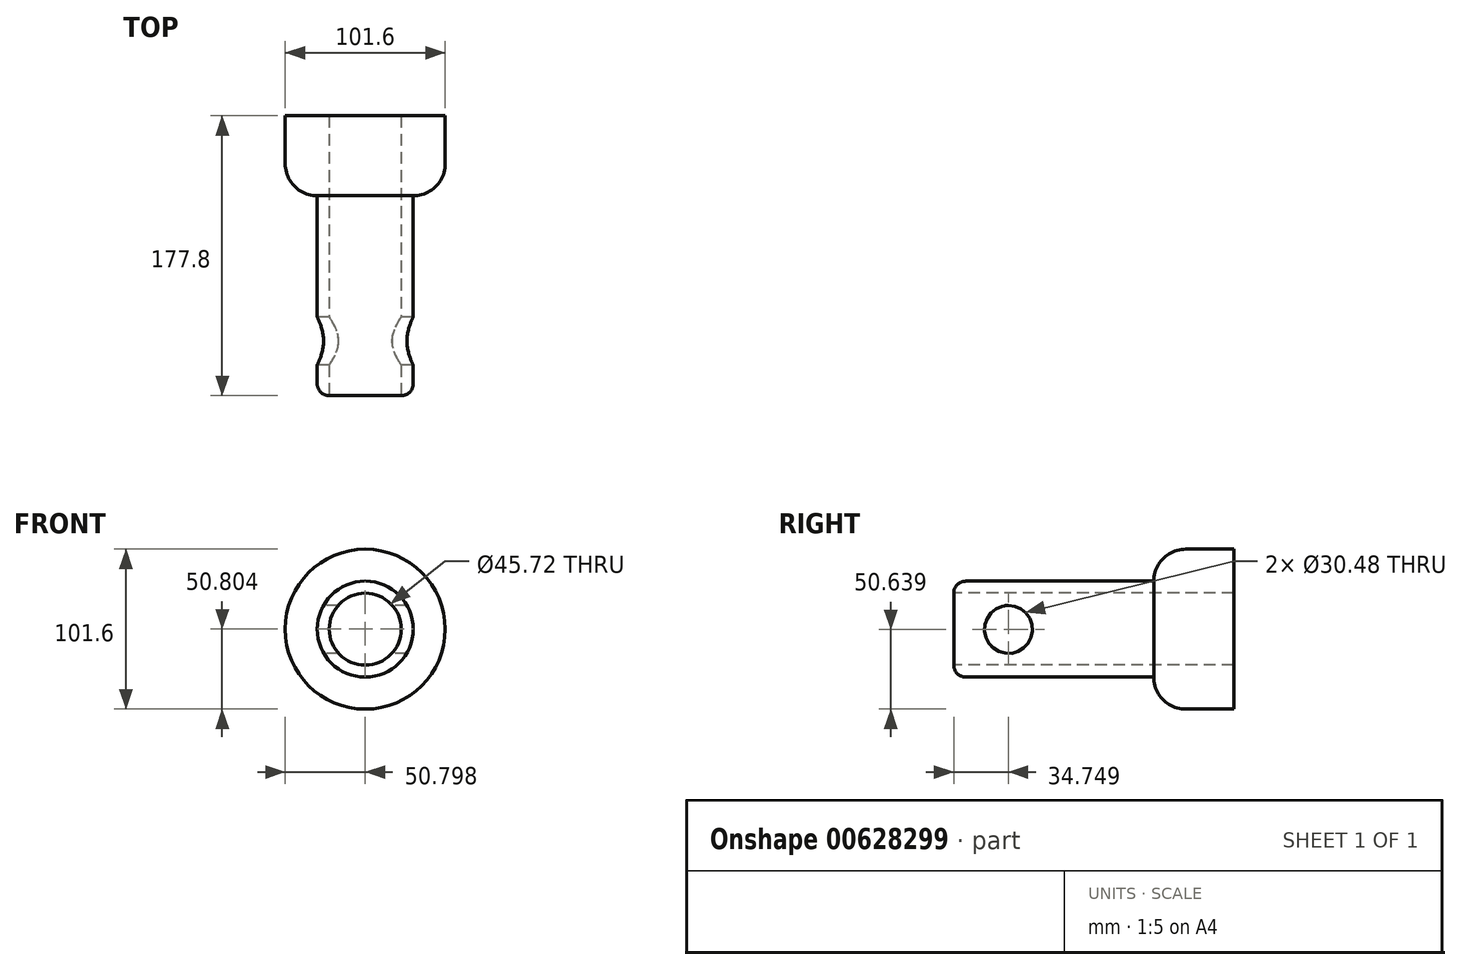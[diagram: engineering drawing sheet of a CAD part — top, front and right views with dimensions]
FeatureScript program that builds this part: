
annotation { "Feature Type Name" : "Feature", "Feature Type Description" : "" }
export const myFeature = defineFeature(function(context is Context, id is Id, definition is map)
    precondition{}
    {
        {
            var Q0;
            Q0=qCreatedBy(makeId("Front.planeOp"),FACE);
            var sketch = newSketch(context, id + "F0", { "sketchPlane" : qUnion([Q0])});
            skCircle(sketch, "E0", {"center": v(-16.63, 18.24) * mm, "radius": 50.8 * mm});
            skSolve(sketch);
        }
        {
            var Q0;
            Q0=makeQuery(id+"F0.imprint","IMPRINT",FACE,{"disambiguationData":[TD([[makeQuery(id+"F0.imprint","IMPRINT",EDGE,{"derivedFrom":sQuery(id+"F0.wireOp",EDGE,"E0")}),1.0]])]});
            extrude(context, id + "F1", {"entities" : qUnion([Q0]), "depth" : 50.8 * mm, "offsetDistance" : 25.4 * mm});
        }
        {
            var Q0;
            Q0=makeQuery(id+"F1.opExtrude","CAP_EDGE",EDGE,{"disambiguationData":[OSD([sQuery(id+"F0.wireOp",EDGE,"E0")])],"isStart":false});
            fillet(context, id + "F2", {"entities" : qUnion([Q0]), "radius" : 20.32 * mm, "tangentPropagation" : true, "allowEdgeOverflow" : false});
        }
        {
            var Q0;
            Q0=makeQuery(id+"F1.opExtrude","CAP_FACE",FACE,{"disambiguationData":[OSD([sQuery(id+"F0.wireOp",EDGE,"E0")])],"isStart":false});
            extrude(context, id + "F3", {"entities" : qUnion([Q0]), "operationType" : NewBodyOperationType.ADD, "depth" : 127 * mm, "offsetDistance" : 25.4 * mm});
        }
        {
            var Q0;
            Q0=makeQuery(id+"F3.opExtrude","CAP_EDGE",EDGE,{"disambiguationData":[OSD([sQuery(id+"F0.wireOp",EDGE,"E0")])],"isStart":false});
            fillet(context, id + "F4", {"entities" : qUnion([Q0]), "radius" : 7.62 * mm, "tangentPropagation" : true, "allowEdgeOverflow" : false});
        }
        {
            var Q0;
            Q0=makeQuery(id+"F3.opExtrude","CAP_FACE",FACE,{"disambiguationData":[OSD([sQuery(id+"F0.wireOp",EDGE,"E0")])],"isStart":false});
            extrude(context, id + "F5", {"entities" : qUnion([Q0]), "operationType" : NewBodyOperationType.REMOVE, "oppositeDirection" : true, "depth" : 231.9 * mm, "offsetDistance" : 25.4 * mm});
        }
        {
            var Q0;
            Q0=qCreatedBy(makeId("Right.planeOp"),FACE);
            var sketch = newSketch(context, id + "F6", { "sketchPlane" : qUnion([Q0])});
            skCircle(sketch, "E1", {"center": v(-143.05, 18.08) * mm, "radius": 15.24 * mm});
            skSolve(sketch);
        }
        {
            var Q0;
            Q0 = qSketchRegion(id + "F6", true);
            extrude(context, id + "F7", {"entities" : qUnion([Q0]), "operationType" : NewBodyOperationType.REMOVE, "depth" : 114.3 * mm, "offsetDistance" : 25.4 * mm, "hasSecondDirection" : true, "secondDirectionOppositeDirection" : true, "secondDirectionDepth" : 213.36 * mm});
        }
    });
